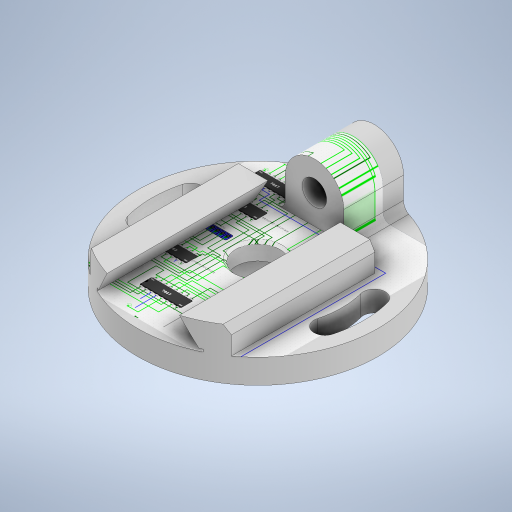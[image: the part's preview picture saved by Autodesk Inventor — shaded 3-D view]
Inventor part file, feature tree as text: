
AUTODESK INVENTOR PART (.ipt)
format: ipt  version: 2023 (Build 270158000, 158)  size: 470,016 bytes
history: native  units: mm
features: extrude x5, sketch x4, chamfer x3, other x2, revolve x1, mirror x1, fillet x1
ambient origin geometry x8: Origin, YZ Plane, XZ Plane, XY Plane, X Axis, Y Axis, Z Axis, Center Point
bodies: Solido1 (feature_tree)
feature tree (17):
  sketch  "Schizzo1"
  revolve  "Rivoluzione1"
  extrude  "Estrusione1"  Depth=197.0mm
  extrude  "Estrusione2"  Depth=185.0mm
  mirror  "Specchio1"
  sketch  "Schizzo2"
  extrude  "Estrusione3"  Depth=116.0mm
  extrude  "Estrusione4"  Depth=88.0mm
  extrude  "Estrusione5"  Depth=67.0mm
  fillet  "Raccordo1"  Radius=58.0mm
  chamfer  "Smusso1"  Distance=87.0mm
  chamfer  "Smusso2"  Distance=36.0mm
  chamfer  "Smusso3"  Distance=12.0mm
  other  "Decalcomania1"
  sketch  "Schizzo3"
  sketch  "Schizzo5"
  other  "Immagine1"
